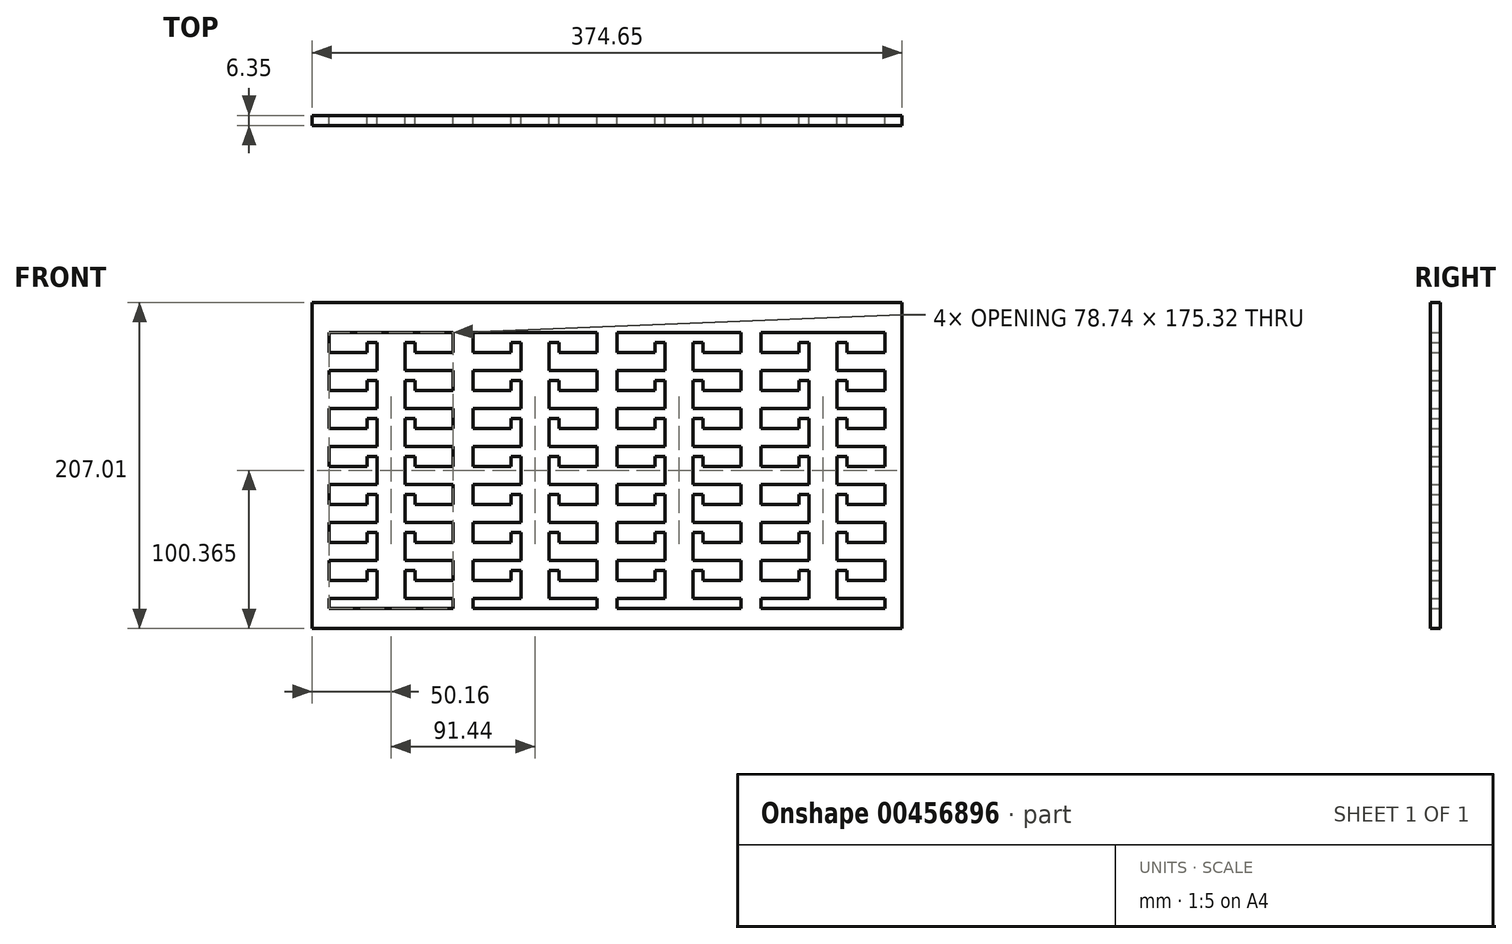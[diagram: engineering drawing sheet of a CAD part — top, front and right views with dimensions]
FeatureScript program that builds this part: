
annotation { "Feature Type Name" : "Feature", "Feature Type Description" : "" }
export const myFeature = defineFeature(function(context is Context, id is Id, definition is map)
    precondition{}
    {
        {
            var Q0;
            Q0=qCreatedBy(makeId("Front.planeOp"),FACE);
            var sketch = newSketch(context, id + "F0", { "sketchPlane" : qUnion([Q0])});
            skLineSegment(sketch, "E0", {"start": v(-92.88, -73.63) * mm, "end": v(-62.4, -73.63) * mm});
            skLineSegment(sketch, "E1", {"start": v(-62.4, -73.63) * mm, "end": v(-62.4, -55.85) * mm});
            skLineSegment(sketch, "E2", {"start": v(-62.4, -55.85) * mm, "end": v(-68.75, -55.85) * mm});
            skLineSegment(sketch, "E3", {"start": v(-68.75, -55.85) * mm, "end": v(-68.75, -62.2) * mm});
            skLineSegment(sketch, "E4", {"start": v(-68.75, -62.2) * mm, "end": v(-92.88, -62.2) * mm});
            skLineSegment(sketch, "E5", {"start": v(-92.88, -62.2) * mm, "end": v(-92.88, -49.5) * mm});
            skLineSegment(sketch, "E6", {"start": v(-92.88, -49.5) * mm, "end": v(-62.4, -49.5) * mm});
            skLineSegment(sketch, "E7", {"start": v(-62.4, -49.5) * mm, "end": v(-62.4, -31.72) * mm});
            skLineSegment(sketch, "E8", {"start": v(-62.4, -31.72) * mm, "end": v(-68.75, -31.72) * mm});
            skLineSegment(sketch, "E9", {"start": v(-68.75, -31.72) * mm, "end": v(-68.75, -38.07) * mm});
            skLineSegment(sketch, "E10", {"start": v(-68.75, -38.07) * mm, "end": v(-92.88, -38.07) * mm});
            skLineSegment(sketch, "E11", {"start": v(-92.88, -38.07) * mm, "end": v(-92.88, -25.37) * mm});
            skLineSegment(sketch, "E12", {"start": v(-92.88, -25.37) * mm, "end": v(-62.4, -25.37) * mm});
            skLineSegment(sketch, "E13", {"start": v(-62.4, -25.37) * mm, "end": v(-62.4, -7.6) * mm});
            skLineSegment(sketch, "E14", {"start": v(-62.4, -7.6) * mm, "end": v(-68.75, -7.6) * mm});
            skLineSegment(sketch, "E15", {"start": v(-68.75, -7.6) * mm, "end": v(-68.75, -13.94) * mm});
            skLineSegment(sketch, "E16", {"start": v(-68.75, -13.94) * mm, "end": v(-92.88, -13.94) * mm});
            skLineSegment(sketch, "E17", {"start": v(-92.88, -13.94) * mm, "end": v(-92.88, -1.24) * mm});
            skLineSegment(sketch, "E18", {"start": v(-92.88, -1.24) * mm, "end": v(-62.4, -1.24) * mm});
            skLineSegment(sketch, "E19", {"start": v(-62.4, -1.24) * mm, "end": v(-62.4, 16.54) * mm});
            skLineSegment(sketch, "E20", {"start": v(-62.4, 16.54) * mm, "end": v(-68.75, 16.54) * mm});
            skLineSegment(sketch, "E21", {"start": v(-68.75, 16.54) * mm, "end": v(-68.75, 10.19) * mm});
            skLineSegment(sketch, "E22", {"start": v(-68.75, 10.19) * mm, "end": v(-92.88, 10.19) * mm});
            skLineSegment(sketch, "E23", {"start": v(-92.88, 10.19) * mm, "end": v(-92.88, 22.89) * mm});
            skLineSegment(sketch, "E24", {"start": v(-92.88, 22.89) * mm, "end": v(-62.4, 22.89) * mm});
            skLineSegment(sketch, "E25", {"start": v(-62.4, 22.89) * mm, "end": v(-62.4, 40.67) * mm});
            skLineSegment(sketch, "E26", {"start": v(-62.4, 40.67) * mm, "end": v(-68.75, 40.67) * mm});
            skLineSegment(sketch, "E27", {"start": v(-68.75, 40.67) * mm, "end": v(-68.75, 34.32) * mm});
            skLineSegment(sketch, "E28", {"start": v(-68.75, 34.32) * mm, "end": v(-92.88, 34.32) * mm});
            skLineSegment(sketch, "E29", {"start": v(-92.88, 34.32) * mm, "end": v(-92.88, 47.02) * mm});
            skLineSegment(sketch, "E30", {"start": v(-92.88, 47.02) * mm, "end": v(-62.4, 47.02) * mm});
            skLineSegment(sketch, "E31", {"start": v(-62.4, 64.8) * mm, "end": v(-68.75, 64.8) * mm});
            skLineSegment(sketch, "E32", {"start": v(-68.75, 64.8) * mm, "end": v(-68.75, 58.45) * mm});
            skLineSegment(sketch, "E33", {"start": v(-68.75, 58.45) * mm, "end": v(-92.88, 58.45) * mm});
            skLineSegment(sketch, "E34", {"start": v(-92.88, 58.45) * mm, "end": v(-92.88, 71.15) * mm});
            skLineSegment(sketch, "E35", {"start": v(-14.14, -104.18) * mm, "end": v(-14.14, -97.76) * mm});
            skLineSegment(sketch, "E36", {"start": v(-14.14, -97.76) * mm, "end": v(-44.62, -97.76) * mm});
            skLineSegment(sketch, "E37", {"start": v(-44.62, -97.76) * mm, "end": v(-44.62, -79.98) * mm});
            skLineSegment(sketch, "E38", {"start": v(-44.62, -79.98) * mm, "end": v(-38.27, -79.98) * mm});
            skLineSegment(sketch, "E39", {"start": v(-38.27, -79.98) * mm, "end": v(-38.27, -86.33) * mm});
            skLineSegment(sketch, "E40", {"start": v(-38.27, -86.33) * mm, "end": v(-14.14, -86.33) * mm});
            skLineSegment(sketch, "E41", {"start": v(-14.14, -86.33) * mm, "end": v(-14.14, -73.63) * mm});
            skLineSegment(sketch, "E42", {"start": v(-14.14, -73.63) * mm, "end": v(-44.62, -73.63) * mm});
            skLineSegment(sketch, "E43", {"start": v(-44.62, -73.63) * mm, "end": v(-44.62, -55.85) * mm});
            skLineSegment(sketch, "E44", {"start": v(-44.62, -55.85) * mm, "end": v(-38.27, -55.85) * mm});
            skLineSegment(sketch, "E45", {"start": v(-38.27, -55.85) * mm, "end": v(-38.27, -62.2) * mm});
            skLineSegment(sketch, "E46", {"start": v(-38.27, -62.2) * mm, "end": v(-14.14, -62.2) * mm});
            skLineSegment(sketch, "E47", {"start": v(-14.14, -62.2) * mm, "end": v(-14.14, -49.5) * mm});
            skLineSegment(sketch, "E48", {"start": v(-14.14, -49.5) * mm, "end": v(-44.62, -49.5) * mm});
            skLineSegment(sketch, "E49", {"start": v(-44.62, -49.5) * mm, "end": v(-44.62, -31.72) * mm});
            skLineSegment(sketch, "E50", {"start": v(-44.62, -31.72) * mm, "end": v(-38.27, -31.72) * mm});
            skLineSegment(sketch, "E51", {"start": v(-38.27, -31.72) * mm, "end": v(-38.27, -38.07) * mm});
            skLineSegment(sketch, "E52", {"start": v(-38.27, -38.07) * mm, "end": v(-14.14, -38.07) * mm});
            skLineSegment(sketch, "E53", {"start": v(-14.14, -38.07) * mm, "end": v(-14.14, -25.37) * mm});
            skLineSegment(sketch, "E54", {"start": v(-14.14, -25.37) * mm, "end": v(-44.62, -25.37) * mm});
            skLineSegment(sketch, "E55", {"start": v(-44.62, -25.37) * mm, "end": v(-44.62, -7.6) * mm});
            skLineSegment(sketch, "E56", {"start": v(-44.62, -7.6) * mm, "end": v(-38.27, -7.6) * mm});
            skLineSegment(sketch, "E57", {"start": v(-38.27, -7.6) * mm, "end": v(-38.27, -13.94) * mm});
            skLineSegment(sketch, "E58", {"start": v(-38.27, -13.94) * mm, "end": v(-14.14, -13.94) * mm});
            skLineSegment(sketch, "E59", {"start": v(-14.14, -13.94) * mm, "end": v(-14.14, -1.24) * mm});
            skLineSegment(sketch, "E60", {"start": v(-14.14, -1.24) * mm, "end": v(-44.62, -1.24) * mm});
            skLineSegment(sketch, "E61", {"start": v(-44.62, -1.24) * mm, "end": v(-44.62, 16.54) * mm});
            skLineSegment(sketch, "E62", {"start": v(-44.62, 16.54) * mm, "end": v(-38.27, 16.54) * mm});
            skLineSegment(sketch, "E63", {"start": v(-38.27, 16.54) * mm, "end": v(-38.27, 10.19) * mm});
            skLineSegment(sketch, "E64", {"start": v(-38.27, 10.19) * mm, "end": v(-14.14, 10.19) * mm});
            skLineSegment(sketch, "E65", {"start": v(-14.14, 10.19) * mm, "end": v(-14.14, 22.89) * mm});
            skLineSegment(sketch, "E66", {"start": v(-14.14, 22.89) * mm, "end": v(-44.62, 22.89) * mm});
            skLineSegment(sketch, "E67", {"start": v(-44.62, 22.89) * mm, "end": v(-44.62, 40.67) * mm});
            skLineSegment(sketch, "E68", {"start": v(-44.62, 40.67) * mm, "end": v(-38.27, 40.67) * mm});
            skLineSegment(sketch, "E69", {"start": v(-38.27, 40.67) * mm, "end": v(-38.27, 34.32) * mm});
            skLineSegment(sketch, "E70", {"start": v(-38.27, 34.32) * mm, "end": v(-14.14, 34.32) * mm});
            skLineSegment(sketch, "E71", {"start": v(-14.14, 34.32) * mm, "end": v(-14.14, 47.02) * mm});
            skLineSegment(sketch, "E72", {"start": v(-14.14, 47.02) * mm, "end": v(-44.62, 47.02) * mm});
            skLineSegment(sketch, "E73", {"start": v(-44.62, 47.02) * mm, "end": v(-44.62, 64.8) * mm});
            skLineSegment(sketch, "E74", {"start": v(-44.62, 64.8) * mm, "end": v(-38.27, 64.8) * mm});
            skLineSegment(sketch, "E75", {"start": v(-38.27, 64.8) * mm, "end": v(-38.27, 58.45) * mm});
            skLineSegment(sketch, "E76", {"start": v(-38.27, 58.45) * mm, "end": v(-14.14, 58.45) * mm});
            skLineSegment(sketch, "E77", {"start": v(-14.14, 58.45) * mm, "end": v(-14.14, 71.15) * mm});
            skLineSegment(sketch, "E78", {"start": v(-62.4, 47.02) * mm, "end": v(-62.4, 64.8) * mm});
            skLineSegment(sketch, "E79", {"start": v(-62.4, -97.76) * mm, "end": v(-62.4, -79.98) * mm});
            skLineSegment(sketch, "E80", {"start": v(-68.75, -86.33) * mm, "end": v(-68.75, -79.98) * mm});
            skLineSegment(sketch, "E81", {"start": v(-68.75, -79.98) * mm, "end": v(-62.4, -79.98) * mm});
            skLineSegment(sketch, "E82", {"start": v(-62.4, -97.76) * mm, "end": v(-92.88, -97.76) * mm});
            skLineSegment(sketch, "E83", {"start": v(-92.88, -86.33) * mm, "end": v(-92.88, -73.63) * mm});
            skLineSegment(sketch, "E84", {"start": v(-92.88, -97.76) * mm, "end": v(-92.88, -104.18) * mm});
            skLineSegment(sketch, "E85", {"start": v(-92.88, -86.33) * mm, "end": v(-68.75, -86.33) * mm});
            skLineSegment(sketch, "E86", {"start": v(-92.88, -104.18) * mm, "end": v(-14.14, -104.18) * mm});
            skLineSegment(sketch, "E87", {"start": v(-92.88, 71.15) * mm, "end": v(-14.14, 71.15) * mm});
            skPoint(sketch, "E88", {"position": v(-53.5, 71.15) * mm});
            skPoint(sketch, "E89", {"position": v(-53.5, -104.18) * mm});
            skLineSegment(sketch, "E90", {"start": v(-184.32, -73.63) * mm, "end": v(-153.84, -73.63) * mm});
            skLineSegment(sketch, "E91", {"start": v(-153.84, -73.63) * mm, "end": v(-153.84, -55.85) * mm});
            skLineSegment(sketch, "E92", {"start": v(-153.84, -55.85) * mm, "end": v(-160.19, -55.85) * mm});
            skLineSegment(sketch, "E93", {"start": v(-160.19, -55.85) * mm, "end": v(-160.19, -62.2) * mm});
            skLineSegment(sketch, "E94", {"start": v(-160.19, -62.2) * mm, "end": v(-184.32, -62.2) * mm});
            skLineSegment(sketch, "E95", {"start": v(-184.32, -62.2) * mm, "end": v(-184.32, -49.5) * mm});
            skLineSegment(sketch, "E96", {"start": v(-184.32, -49.5) * mm, "end": v(-153.84, -49.5) * mm});
            skLineSegment(sketch, "E97", {"start": v(-153.84, -49.5) * mm, "end": v(-153.84, -31.72) * mm});
            skLineSegment(sketch, "E98", {"start": v(-153.84, -31.72) * mm, "end": v(-160.19, -31.72) * mm});
            skLineSegment(sketch, "E99", {"start": v(-160.19, -31.72) * mm, "end": v(-160.19, -38.07) * mm});
            skLineSegment(sketch, "E100", {"start": v(-160.19, -38.07) * mm, "end": v(-184.32, -38.07) * mm});
            skLineSegment(sketch, "E101", {"start": v(-184.32, -38.07) * mm, "end": v(-184.32, -25.37) * mm});
            skLineSegment(sketch, "E102", {"start": v(-184.32, -25.37) * mm, "end": v(-153.84, -25.37) * mm});
            skLineSegment(sketch, "E103", {"start": v(-153.84, -25.37) * mm, "end": v(-153.84, -7.6) * mm});
            skLineSegment(sketch, "E104", {"start": v(-153.84, -7.6) * mm, "end": v(-160.19, -7.6) * mm});
            skLineSegment(sketch, "E105", {"start": v(-160.19, -7.6) * mm, "end": v(-160.19, -13.94) * mm});
            skLineSegment(sketch, "E106", {"start": v(-160.19, -13.94) * mm, "end": v(-184.32, -13.94) * mm});
            skLineSegment(sketch, "E107", {"start": v(-184.32, -13.94) * mm, "end": v(-184.32, -1.24) * mm});
            skLineSegment(sketch, "E108", {"start": v(-184.32, -1.24) * mm, "end": v(-153.84, -1.24) * mm});
            skLineSegment(sketch, "E109", {"start": v(-153.84, -1.24) * mm, "end": v(-153.84, 16.54) * mm});
            skLineSegment(sketch, "E110", {"start": v(-153.84, 16.54) * mm, "end": v(-160.19, 16.54) * mm});
            skLineSegment(sketch, "E111", {"start": v(-160.19, 16.54) * mm, "end": v(-160.19, 10.19) * mm});
            skLineSegment(sketch, "E112", {"start": v(-160.19, 10.19) * mm, "end": v(-184.32, 10.19) * mm});
            skLineSegment(sketch, "E113", {"start": v(-184.32, 10.19) * mm, "end": v(-184.32, 22.89) * mm});
            skLineSegment(sketch, "E114", {"start": v(-184.32, 22.89) * mm, "end": v(-153.84, 22.89) * mm});
            skLineSegment(sketch, "E115", {"start": v(-153.84, 22.89) * mm, "end": v(-153.84, 40.67) * mm});
            skLineSegment(sketch, "E116", {"start": v(-153.84, 40.67) * mm, "end": v(-160.19, 40.67) * mm});
            skLineSegment(sketch, "E117", {"start": v(-160.19, 40.67) * mm, "end": v(-160.19, 34.32) * mm});
            skLineSegment(sketch, "E118", {"start": v(-160.19, 34.32) * mm, "end": v(-184.32, 34.32) * mm});
            skLineSegment(sketch, "E119", {"start": v(-184.32, 34.32) * mm, "end": v(-184.32, 47.02) * mm});
            skLineSegment(sketch, "E120", {"start": v(-184.32, 47.02) * mm, "end": v(-153.84, 47.02) * mm});
            skLineSegment(sketch, "E121", {"start": v(-153.84, 64.8) * mm, "end": v(-160.19, 64.8) * mm});
            skLineSegment(sketch, "E122", {"start": v(-160.19, 64.8) * mm, "end": v(-160.19, 58.45) * mm});
            skLineSegment(sketch, "E123", {"start": v(-160.19, 58.45) * mm, "end": v(-184.32, 58.45) * mm});
            skLineSegment(sketch, "E124", {"start": v(-184.32, 58.45) * mm, "end": v(-184.32, 71.15) * mm});
            skLineSegment(sketch, "E125", {"start": v(-105.58, -104.18) * mm, "end": v(-105.58, -97.76) * mm});
            skLineSegment(sketch, "E126", {"start": v(-105.58, -97.76) * mm, "end": v(-136.06, -97.76) * mm});
            skLineSegment(sketch, "E127", {"start": v(-136.06, -97.76) * mm, "end": v(-136.06, -79.98) * mm});
            skLineSegment(sketch, "E128", {"start": v(-136.06, -79.98) * mm, "end": v(-129.7, -79.98) * mm});
            skLineSegment(sketch, "E129", {"start": v(-129.7, -79.98) * mm, "end": v(-129.7, -86.33) * mm});
            skLineSegment(sketch, "E130", {"start": v(-129.7, -86.33) * mm, "end": v(-105.58, -86.33) * mm});
            skLineSegment(sketch, "E131", {"start": v(-105.58, -86.33) * mm, "end": v(-105.58, -73.63) * mm});
            skLineSegment(sketch, "E132", {"start": v(-105.58, -73.63) * mm, "end": v(-136.06, -73.63) * mm});
            skLineSegment(sketch, "E133", {"start": v(-136.06, -73.63) * mm, "end": v(-136.06, -55.85) * mm});
            skLineSegment(sketch, "E134", {"start": v(-136.06, -55.85) * mm, "end": v(-129.7, -55.85) * mm});
            skLineSegment(sketch, "E135", {"start": v(-129.7, -55.85) * mm, "end": v(-129.7, -62.2) * mm});
            skLineSegment(sketch, "E136", {"start": v(-129.7, -62.2) * mm, "end": v(-105.58, -62.2) * mm});
            skLineSegment(sketch, "E137", {"start": v(-105.58, -62.2) * mm, "end": v(-105.58, -49.5) * mm});
            skLineSegment(sketch, "E138", {"start": v(-105.58, -49.5) * mm, "end": v(-136.06, -49.5) * mm});
            skLineSegment(sketch, "E139", {"start": v(-136.06, -49.5) * mm, "end": v(-136.06, -31.72) * mm});
            skLineSegment(sketch, "E140", {"start": v(-136.06, -31.72) * mm, "end": v(-129.7, -31.72) * mm});
            skLineSegment(sketch, "E141", {"start": v(-129.7, -31.72) * mm, "end": v(-129.7, -38.07) * mm});
            skLineSegment(sketch, "E142", {"start": v(-129.7, -38.07) * mm, "end": v(-105.58, -38.07) * mm});
            skLineSegment(sketch, "E143", {"start": v(-105.58, -38.07) * mm, "end": v(-105.58, -25.37) * mm});
            skLineSegment(sketch, "E144", {"start": v(-105.58, -25.37) * mm, "end": v(-136.06, -25.37) * mm});
            skLineSegment(sketch, "E145", {"start": v(-136.06, -25.37) * mm, "end": v(-136.06, -7.6) * mm});
            skLineSegment(sketch, "E146", {"start": v(-136.06, -7.6) * mm, "end": v(-129.7, -7.6) * mm});
            skLineSegment(sketch, "E147", {"start": v(-129.7, -7.6) * mm, "end": v(-129.7, -13.94) * mm});
            skLineSegment(sketch, "E148", {"start": v(-129.7, -13.94) * mm, "end": v(-105.58, -13.94) * mm});
            skLineSegment(sketch, "E149", {"start": v(-105.58, -13.94) * mm, "end": v(-105.58, -1.24) * mm});
            skLineSegment(sketch, "E150", {"start": v(-105.58, -1.24) * mm, "end": v(-136.06, -1.24) * mm});
            skLineSegment(sketch, "E151", {"start": v(-136.06, -1.24) * mm, "end": v(-136.06, 16.54) * mm});
            skLineSegment(sketch, "E152", {"start": v(-136.06, 16.54) * mm, "end": v(-129.7, 16.54) * mm});
            skLineSegment(sketch, "E153", {"start": v(-129.7, 16.54) * mm, "end": v(-129.7, 10.19) * mm});
            skLineSegment(sketch, "E154", {"start": v(-129.7, 10.19) * mm, "end": v(-105.58, 10.19) * mm});
            skLineSegment(sketch, "E155", {"start": v(-105.58, 10.19) * mm, "end": v(-105.58, 22.89) * mm});
            skLineSegment(sketch, "E156", {"start": v(-105.58, 22.89) * mm, "end": v(-136.06, 22.89) * mm});
            skLineSegment(sketch, "E157", {"start": v(-136.06, 22.89) * mm, "end": v(-136.06, 40.67) * mm});
            skLineSegment(sketch, "E158", {"start": v(-136.06, 40.67) * mm, "end": v(-129.7, 40.67) * mm});
            skLineSegment(sketch, "E159", {"start": v(-129.7, 40.67) * mm, "end": v(-129.7, 34.32) * mm});
            skLineSegment(sketch, "E160", {"start": v(-129.7, 34.32) * mm, "end": v(-105.58, 34.32) * mm});
            skLineSegment(sketch, "E161", {"start": v(-105.58, 34.32) * mm, "end": v(-105.58, 47.02) * mm});
            skLineSegment(sketch, "E162", {"start": v(-105.58, 47.02) * mm, "end": v(-136.06, 47.02) * mm});
            skLineSegment(sketch, "E163", {"start": v(-136.06, 47.02) * mm, "end": v(-136.06, 64.8) * mm});
            skLineSegment(sketch, "E164", {"start": v(-136.06, 64.8) * mm, "end": v(-129.7, 64.8) * mm});
            skLineSegment(sketch, "E165", {"start": v(-129.7, 64.8) * mm, "end": v(-129.7, 58.45) * mm});
            skLineSegment(sketch, "E166", {"start": v(-129.7, 58.45) * mm, "end": v(-105.58, 58.45) * mm});
            skLineSegment(sketch, "E167", {"start": v(-105.58, 58.45) * mm, "end": v(-105.58, 71.15) * mm});
            skLineSegment(sketch, "E168", {"start": v(-153.84, 47.02) * mm, "end": v(-153.84, 64.8) * mm});
            skLineSegment(sketch, "E169", {"start": v(-153.84, -97.76) * mm, "end": v(-153.84, -79.98) * mm});
            skLineSegment(sketch, "E170", {"start": v(-160.19, -86.33) * mm, "end": v(-160.19, -79.98) * mm});
            skLineSegment(sketch, "E171", {"start": v(-160.19, -79.98) * mm, "end": v(-153.84, -79.98) * mm});
            skLineSegment(sketch, "E172", {"start": v(-153.84, -97.76) * mm, "end": v(-184.32, -97.76) * mm});
            skLineSegment(sketch, "E173", {"start": v(-184.32, -86.33) * mm, "end": v(-184.32, -73.63) * mm});
            skLineSegment(sketch, "E174", {"start": v(-184.32, -97.76) * mm, "end": v(-184.32, -104.18) * mm});
            skLineSegment(sketch, "E175", {"start": v(-184.32, -86.33) * mm, "end": v(-160.19, -86.33) * mm});
            skLineSegment(sketch, "E176", {"start": v(-184.32, -104.18) * mm, "end": v(-105.58, -104.18) * mm});
            skLineSegment(sketch, "E177", {"start": v(-184.32, 71.15) * mm, "end": v(-105.58, 71.15) * mm});
            skPoint(sketch, "E178", {"position": v(-144.95, 71.15) * mm});
            skPoint(sketch, "E179", {"position": v(-144.95, -104.18) * mm});
            skLineSegment(sketch, "E180", {"start": v(-275.76, -73.63) * mm, "end": v(-245.28, -73.63) * mm});
            skLineSegment(sketch, "E181", {"start": v(-245.28, -73.63) * mm, "end": v(-245.28, -55.85) * mm});
            skLineSegment(sketch, "E182", {"start": v(-245.28, -55.85) * mm, "end": v(-251.63, -55.85) * mm});
            skLineSegment(sketch, "E183", {"start": v(-251.63, -55.85) * mm, "end": v(-251.63, -62.2) * mm});
            skLineSegment(sketch, "E184", {"start": v(-251.63, -62.2) * mm, "end": v(-275.76, -62.2) * mm});
            skLineSegment(sketch, "E185", {"start": v(-275.76, -62.2) * mm, "end": v(-275.76, -49.5) * mm});
            skLineSegment(sketch, "E186", {"start": v(-275.76, -49.5) * mm, "end": v(-245.28, -49.5) * mm});
            skLineSegment(sketch, "E187", {"start": v(-245.28, -49.5) * mm, "end": v(-245.28, -31.72) * mm});
            skLineSegment(sketch, "E188", {"start": v(-245.28, -31.72) * mm, "end": v(-251.63, -31.72) * mm});
            skLineSegment(sketch, "E189", {"start": v(-251.63, -31.72) * mm, "end": v(-251.63, -38.07) * mm});
            skLineSegment(sketch, "E190", {"start": v(-251.63, -38.07) * mm, "end": v(-275.76, -38.07) * mm});
            skLineSegment(sketch, "E191", {"start": v(-275.76, -38.07) * mm, "end": v(-275.76, -25.37) * mm});
            skLineSegment(sketch, "E192", {"start": v(-275.76, -25.37) * mm, "end": v(-245.28, -25.37) * mm});
            skLineSegment(sketch, "E193", {"start": v(-245.28, -25.37) * mm, "end": v(-245.28, -7.6) * mm});
            skLineSegment(sketch, "E194", {"start": v(-245.28, -7.6) * mm, "end": v(-251.63, -7.6) * mm});
            skLineSegment(sketch, "E195", {"start": v(-251.63, -7.6) * mm, "end": v(-251.63, -13.94) * mm});
            skLineSegment(sketch, "E196", {"start": v(-251.63, -13.94) * mm, "end": v(-275.76, -13.94) * mm});
            skLineSegment(sketch, "E197", {"start": v(-275.76, -13.94) * mm, "end": v(-275.76, -1.24) * mm});
            skLineSegment(sketch, "E198", {"start": v(-275.76, -1.24) * mm, "end": v(-245.28, -1.24) * mm});
            skLineSegment(sketch, "E199", {"start": v(-245.28, -1.24) * mm, "end": v(-245.28, 16.54) * mm});
            skLineSegment(sketch, "E200", {"start": v(-245.28, 16.54) * mm, "end": v(-251.63, 16.54) * mm});
            skLineSegment(sketch, "E201", {"start": v(-251.63, 16.54) * mm, "end": v(-251.63, 10.19) * mm});
            skLineSegment(sketch, "E202", {"start": v(-251.63, 10.19) * mm, "end": v(-275.76, 10.19) * mm});
            skLineSegment(sketch, "E203", {"start": v(-275.76, 10.19) * mm, "end": v(-275.76, 22.89) * mm});
            skLineSegment(sketch, "E204", {"start": v(-275.76, 22.89) * mm, "end": v(-245.28, 22.89) * mm});
            skLineSegment(sketch, "E205", {"start": v(-245.28, 22.89) * mm, "end": v(-245.28, 40.67) * mm});
            skLineSegment(sketch, "E206", {"start": v(-245.28, 40.67) * mm, "end": v(-251.63, 40.67) * mm});
            skLineSegment(sketch, "E207", {"start": v(-251.63, 40.67) * mm, "end": v(-251.63, 34.32) * mm});
            skLineSegment(sketch, "E208", {"start": v(-251.63, 34.32) * mm, "end": v(-275.76, 34.32) * mm});
            skLineSegment(sketch, "E209", {"start": v(-275.76, 34.32) * mm, "end": v(-275.76, 47.02) * mm});
            skLineSegment(sketch, "E210", {"start": v(-275.76, 47.02) * mm, "end": v(-245.28, 47.02) * mm});
            skLineSegment(sketch, "E211", {"start": v(-245.28, 64.8) * mm, "end": v(-251.63, 64.8) * mm});
            skLineSegment(sketch, "E212", {"start": v(-251.63, 64.8) * mm, "end": v(-251.63, 58.45) * mm});
            skLineSegment(sketch, "E213", {"start": v(-251.63, 58.45) * mm, "end": v(-275.76, 58.45) * mm});
            skLineSegment(sketch, "E214", {"start": v(-275.76, 58.45) * mm, "end": v(-275.76, 71.15) * mm});
            skLineSegment(sketch, "E215", {"start": v(-197.02, -104.18) * mm, "end": v(-197.02, -97.76) * mm});
            skLineSegment(sketch, "E216", {"start": v(-197.02, -97.76) * mm, "end": v(-227.5, -97.76) * mm});
            skLineSegment(sketch, "E217", {"start": v(-227.5, -97.76) * mm, "end": v(-227.5, -79.98) * mm});
            skLineSegment(sketch, "E218", {"start": v(-227.5, -79.98) * mm, "end": v(-221.15, -79.98) * mm});
            skLineSegment(sketch, "E219", {"start": v(-221.15, -79.98) * mm, "end": v(-221.15, -86.33) * mm});
            skLineSegment(sketch, "E220", {"start": v(-221.15, -86.33) * mm, "end": v(-197.02, -86.33) * mm});
            skLineSegment(sketch, "E221", {"start": v(-197.02, -86.33) * mm, "end": v(-197.02, -73.63) * mm});
            skLineSegment(sketch, "E222", {"start": v(-197.02, -73.63) * mm, "end": v(-227.5, -73.63) * mm});
            skLineSegment(sketch, "E223", {"start": v(-227.5, -73.63) * mm, "end": v(-227.5, -55.85) * mm});
            skLineSegment(sketch, "E224", {"start": v(-227.5, -55.85) * mm, "end": v(-221.15, -55.85) * mm});
            skLineSegment(sketch, "E225", {"start": v(-221.15, -55.85) * mm, "end": v(-221.15, -62.2) * mm});
            skLineSegment(sketch, "E226", {"start": v(-221.15, -62.2) * mm, "end": v(-197.02, -62.2) * mm});
            skLineSegment(sketch, "E227", {"start": v(-197.02, -62.2) * mm, "end": v(-197.02, -49.5) * mm});
            skLineSegment(sketch, "E228", {"start": v(-197.02, -49.5) * mm, "end": v(-227.5, -49.5) * mm});
            skLineSegment(sketch, "E229", {"start": v(-227.5, -49.5) * mm, "end": v(-227.5, -31.72) * mm});
            skLineSegment(sketch, "E230", {"start": v(-227.5, -31.72) * mm, "end": v(-221.15, -31.72) * mm});
            skLineSegment(sketch, "E231", {"start": v(-221.15, -31.72) * mm, "end": v(-221.15, -38.07) * mm});
            skLineSegment(sketch, "E232", {"start": v(-221.15, -38.07) * mm, "end": v(-197.02, -38.07) * mm});
            skLineSegment(sketch, "E233", {"start": v(-197.02, -38.07) * mm, "end": v(-197.02, -25.37) * mm});
            skLineSegment(sketch, "E234", {"start": v(-197.02, -25.37) * mm, "end": v(-227.5, -25.37) * mm});
            skLineSegment(sketch, "E235", {"start": v(-227.5, -25.37) * mm, "end": v(-227.5, -7.6) * mm});
            skLineSegment(sketch, "E236", {"start": v(-227.5, -7.6) * mm, "end": v(-221.15, -7.6) * mm});
            skLineSegment(sketch, "E237", {"start": v(-221.15, -7.6) * mm, "end": v(-221.15, -13.94) * mm});
            skLineSegment(sketch, "E238", {"start": v(-221.15, -13.94) * mm, "end": v(-197.02, -13.94) * mm});
            skLineSegment(sketch, "E239", {"start": v(-197.02, -13.94) * mm, "end": v(-197.02, -1.24) * mm});
            skLineSegment(sketch, "E240", {"start": v(-197.02, -1.24) * mm, "end": v(-227.5, -1.24) * mm});
            skLineSegment(sketch, "E241", {"start": v(-227.5, -1.24) * mm, "end": v(-227.5, 16.54) * mm});
            skLineSegment(sketch, "E242", {"start": v(-227.5, 16.54) * mm, "end": v(-221.15, 16.54) * mm});
            skLineSegment(sketch, "E243", {"start": v(-221.15, 16.54) * mm, "end": v(-221.15, 10.19) * mm});
            skLineSegment(sketch, "E244", {"start": v(-221.15, 10.19) * mm, "end": v(-197.02, 10.19) * mm});
            skLineSegment(sketch, "E245", {"start": v(-197.02, 10.19) * mm, "end": v(-197.02, 22.89) * mm});
            skLineSegment(sketch, "E246", {"start": v(-197.02, 22.89) * mm, "end": v(-227.5, 22.89) * mm});
            skLineSegment(sketch, "E247", {"start": v(-227.5, 22.89) * mm, "end": v(-227.5, 40.67) * mm});
            skLineSegment(sketch, "E248", {"start": v(-227.5, 40.67) * mm, "end": v(-221.15, 40.67) * mm});
            skLineSegment(sketch, "E249", {"start": v(-221.15, 40.67) * mm, "end": v(-221.15, 34.32) * mm});
            skLineSegment(sketch, "E250", {"start": v(-221.15, 34.32) * mm, "end": v(-197.02, 34.32) * mm});
            skLineSegment(sketch, "E251", {"start": v(-197.02, 34.32) * mm, "end": v(-197.02, 47.02) * mm});
            skLineSegment(sketch, "E252", {"start": v(-197.02, 47.02) * mm, "end": v(-227.5, 47.02) * mm});
            skLineSegment(sketch, "E253", {"start": v(-227.5, 47.02) * mm, "end": v(-227.5, 64.8) * mm});
            skLineSegment(sketch, "E254", {"start": v(-227.5, 64.8) * mm, "end": v(-221.15, 64.8) * mm});
            skLineSegment(sketch, "E255", {"start": v(-221.15, 64.8) * mm, "end": v(-221.15, 58.45) * mm});
            skLineSegment(sketch, "E256", {"start": v(-221.15, 58.45) * mm, "end": v(-197.02, 58.45) * mm});
            skLineSegment(sketch, "E257", {"start": v(-197.02, 58.45) * mm, "end": v(-197.02, 71.15) * mm});
            skLineSegment(sketch, "E258", {"start": v(-245.28, 47.02) * mm, "end": v(-245.28, 64.8) * mm});
            skLineSegment(sketch, "E259", {"start": v(-245.28, -97.76) * mm, "end": v(-245.28, -79.98) * mm});
            skLineSegment(sketch, "E260", {"start": v(-251.63, -86.33) * mm, "end": v(-251.63, -79.98) * mm});
            skLineSegment(sketch, "E261", {"start": v(-251.63, -79.98) * mm, "end": v(-245.28, -79.98) * mm});
            skLineSegment(sketch, "E262", {"start": v(-245.28, -97.76) * mm, "end": v(-275.76, -97.76) * mm});
            skLineSegment(sketch, "E263", {"start": v(-275.76, -86.33) * mm, "end": v(-275.76, -73.63) * mm});
            skLineSegment(sketch, "E264", {"start": v(-275.76, -97.76) * mm, "end": v(-275.76, -104.18) * mm});
            skLineSegment(sketch, "E265", {"start": v(-275.76, -86.33) * mm, "end": v(-251.63, -86.33) * mm});
            skLineSegment(sketch, "E266", {"start": v(-275.76, -104.18) * mm, "end": v(-197.02, -104.18) * mm});
            skLineSegment(sketch, "E267", {"start": v(-275.76, 71.15) * mm, "end": v(-197.02, 71.15) * mm});
            skPoint(sketch, "E268", {"position": v(-236.39, 71.15) * mm});
            skPoint(sketch, "E269", {"position": v(-236.39, -104.18) * mm});
            skLineSegment(sketch, "E270", {"start": v(-367.2, -73.63) * mm, "end": v(-336.72, -73.63) * mm});
            skLineSegment(sketch, "E271", {"start": v(-336.72, -73.63) * mm, "end": v(-336.72, -55.85) * mm});
            skLineSegment(sketch, "E272", {"start": v(-336.72, -55.85) * mm, "end": v(-343.07, -55.85) * mm});
            skLineSegment(sketch, "E273", {"start": v(-343.07, -55.85) * mm, "end": v(-343.07, -62.2) * mm});
            skLineSegment(sketch, "E274", {"start": v(-343.07, -62.2) * mm, "end": v(-367.2, -62.2) * mm});
            skLineSegment(sketch, "E275", {"start": v(-367.2, -62.2) * mm, "end": v(-367.2, -49.5) * mm});
            skLineSegment(sketch, "E276", {"start": v(-367.2, -49.5) * mm, "end": v(-336.72, -49.5) * mm});
            skLineSegment(sketch, "E277", {"start": v(-336.72, -49.5) * mm, "end": v(-336.72, -31.72) * mm});
            skLineSegment(sketch, "E278", {"start": v(-336.72, -31.72) * mm, "end": v(-343.07, -31.72) * mm});
            skLineSegment(sketch, "E279", {"start": v(-343.07, -31.72) * mm, "end": v(-343.07, -38.07) * mm});
            skLineSegment(sketch, "E280", {"start": v(-343.07, -38.07) * mm, "end": v(-367.2, -38.07) * mm});
            skLineSegment(sketch, "E281", {"start": v(-367.2, -38.07) * mm, "end": v(-367.2, -25.37) * mm});
            skLineSegment(sketch, "E282", {"start": v(-367.2, -25.37) * mm, "end": v(-336.72, -25.37) * mm});
            skLineSegment(sketch, "E283", {"start": v(-336.72, -25.37) * mm, "end": v(-336.72, -7.6) * mm});
            skLineSegment(sketch, "E284", {"start": v(-336.72, -7.6) * mm, "end": v(-343.07, -7.6) * mm});
            skLineSegment(sketch, "E285", {"start": v(-343.07, -7.6) * mm, "end": v(-343.07, -13.94) * mm});
            skLineSegment(sketch, "E286", {"start": v(-343.07, -13.94) * mm, "end": v(-367.2, -13.94) * mm});
            skLineSegment(sketch, "E287", {"start": v(-367.2, -13.94) * mm, "end": v(-367.2, -1.24) * mm});
            skLineSegment(sketch, "E288", {"start": v(-367.2, -1.24) * mm, "end": v(-336.72, -1.24) * mm});
            skLineSegment(sketch, "E289", {"start": v(-336.72, -1.24) * mm, "end": v(-336.72, 16.54) * mm});
            skLineSegment(sketch, "E290", {"start": v(-336.72, 16.54) * mm, "end": v(-343.07, 16.54) * mm});
            skLineSegment(sketch, "E291", {"start": v(-343.07, 16.54) * mm, "end": v(-343.07, 10.19) * mm});
            skLineSegment(sketch, "E292", {"start": v(-343.07, 10.19) * mm, "end": v(-367.2, 10.19) * mm});
            skLineSegment(sketch, "E293", {"start": v(-367.2, 10.19) * mm, "end": v(-367.2, 22.89) * mm});
            skLineSegment(sketch, "E294", {"start": v(-367.2, 22.89) * mm, "end": v(-336.72, 22.89) * mm});
            skLineSegment(sketch, "E295", {"start": v(-336.72, 22.89) * mm, "end": v(-336.72, 40.67) * mm});
            skLineSegment(sketch, "E296", {"start": v(-336.72, 40.67) * mm, "end": v(-343.07, 40.67) * mm});
            skLineSegment(sketch, "E297", {"start": v(-343.07, 40.67) * mm, "end": v(-343.07, 34.32) * mm});
            skLineSegment(sketch, "E298", {"start": v(-343.07, 34.32) * mm, "end": v(-367.2, 34.32) * mm});
            skLineSegment(sketch, "E299", {"start": v(-367.2, 34.32) * mm, "end": v(-367.2, 47.02) * mm});
            skLineSegment(sketch, "E300", {"start": v(-367.2, 47.02) * mm, "end": v(-336.72, 47.02) * mm});
            skLineSegment(sketch, "E301", {"start": v(-336.72, 64.8) * mm, "end": v(-343.07, 64.8) * mm});
            skLineSegment(sketch, "E302", {"start": v(-343.07, 64.8) * mm, "end": v(-343.07, 58.45) * mm});
            skLineSegment(sketch, "E303", {"start": v(-343.07, 58.45) * mm, "end": v(-367.2, 58.45) * mm});
            skLineSegment(sketch, "E304", {"start": v(-367.2, 58.45) * mm, "end": v(-367.2, 71.15) * mm});
            skLineSegment(sketch, "E305", {"start": v(-288.46, -104.18) * mm, "end": v(-288.46, -97.76) * mm});
            skLineSegment(sketch, "E306", {"start": v(-288.46, -97.76) * mm, "end": v(-318.94, -97.76) * mm});
            skLineSegment(sketch, "E307", {"start": v(-318.94, -97.76) * mm, "end": v(-318.94, -79.98) * mm});
            skLineSegment(sketch, "E308", {"start": v(-318.94, -79.98) * mm, "end": v(-312.59, -79.98) * mm});
            skLineSegment(sketch, "E309", {"start": v(-312.59, -79.98) * mm, "end": v(-312.59, -86.33) * mm});
            skLineSegment(sketch, "E310", {"start": v(-312.59, -86.33) * mm, "end": v(-288.46, -86.33) * mm});
            skLineSegment(sketch, "E311", {"start": v(-288.46, -86.33) * mm, "end": v(-288.46, -73.63) * mm});
            skLineSegment(sketch, "E312", {"start": v(-288.46, -73.63) * mm, "end": v(-318.94, -73.63) * mm});
            skLineSegment(sketch, "E313", {"start": v(-318.94, -73.63) * mm, "end": v(-318.94, -55.85) * mm});
            skLineSegment(sketch, "E314", {"start": v(-318.94, -55.85) * mm, "end": v(-312.59, -55.85) * mm});
            skLineSegment(sketch, "E315", {"start": v(-312.59, -55.85) * mm, "end": v(-312.59, -62.2) * mm});
            skLineSegment(sketch, "E316", {"start": v(-312.59, -62.2) * mm, "end": v(-288.46, -62.2) * mm});
            skLineSegment(sketch, "E317", {"start": v(-288.46, -62.2) * mm, "end": v(-288.46, -49.5) * mm});
            skLineSegment(sketch, "E318", {"start": v(-288.46, -49.5) * mm, "end": v(-318.94, -49.5) * mm});
            skLineSegment(sketch, "E319", {"start": v(-318.94, -49.5) * mm, "end": v(-318.94, -31.72) * mm});
            skLineSegment(sketch, "E320", {"start": v(-318.94, -31.72) * mm, "end": v(-312.59, -31.72) * mm});
            skLineSegment(sketch, "E321", {"start": v(-312.59, -31.72) * mm, "end": v(-312.59, -38.07) * mm});
            skLineSegment(sketch, "E322", {"start": v(-312.59, -38.07) * mm, "end": v(-288.46, -38.07) * mm});
            skLineSegment(sketch, "E323", {"start": v(-288.46, -38.07) * mm, "end": v(-288.46, -25.37) * mm});
            skLineSegment(sketch, "E324", {"start": v(-288.46, -25.37) * mm, "end": v(-318.94, -25.37) * mm});
            skLineSegment(sketch, "E325", {"start": v(-318.94, -25.37) * mm, "end": v(-318.94, -7.6) * mm});
            skLineSegment(sketch, "E326", {"start": v(-318.94, -7.6) * mm, "end": v(-312.59, -7.6) * mm});
            skLineSegment(sketch, "E327", {"start": v(-312.59, -7.6) * mm, "end": v(-312.59, -13.94) * mm});
            skLineSegment(sketch, "E328", {"start": v(-312.59, -13.94) * mm, "end": v(-288.46, -13.94) * mm});
            skLineSegment(sketch, "E329", {"start": v(-288.46, -13.94) * mm, "end": v(-288.46, -1.24) * mm});
            skLineSegment(sketch, "E330", {"start": v(-288.46, -1.24) * mm, "end": v(-318.94, -1.24) * mm});
            skLineSegment(sketch, "E331", {"start": v(-318.94, -1.24) * mm, "end": v(-318.94, 16.54) * mm});
            skLineSegment(sketch, "E332", {"start": v(-318.94, 16.54) * mm, "end": v(-312.59, 16.54) * mm});
            skLineSegment(sketch, "E333", {"start": v(-312.59, 16.54) * mm, "end": v(-312.59, 10.19) * mm});
            skLineSegment(sketch, "E334", {"start": v(-312.59, 10.19) * mm, "end": v(-288.46, 10.19) * mm});
            skLineSegment(sketch, "E335", {"start": v(-288.46, 10.19) * mm, "end": v(-288.46, 22.89) * mm});
            skLineSegment(sketch, "E336", {"start": v(-288.46, 22.89) * mm, "end": v(-318.94, 22.89) * mm});
            skLineSegment(sketch, "E337", {"start": v(-318.94, 22.89) * mm, "end": v(-318.94, 40.67) * mm});
            skLineSegment(sketch, "E338", {"start": v(-318.94, 40.67) * mm, "end": v(-312.59, 40.67) * mm});
            skLineSegment(sketch, "E339", {"start": v(-312.59, 40.67) * mm, "end": v(-312.59, 34.32) * mm});
            skLineSegment(sketch, "E340", {"start": v(-312.59, 34.32) * mm, "end": v(-288.46, 34.32) * mm});
            skLineSegment(sketch, "E341", {"start": v(-288.46, 34.32) * mm, "end": v(-288.46, 47.02) * mm});
            skLineSegment(sketch, "E342", {"start": v(-288.46, 47.02) * mm, "end": v(-318.94, 47.02) * mm});
            skLineSegment(sketch, "E343", {"start": v(-318.94, 47.02) * mm, "end": v(-318.94, 64.8) * mm});
            skLineSegment(sketch, "E344", {"start": v(-318.94, 64.8) * mm, "end": v(-312.59, 64.8) * mm});
            skLineSegment(sketch, "E345", {"start": v(-312.59, 64.8) * mm, "end": v(-312.59, 58.45) * mm});
            skLineSegment(sketch, "E346", {"start": v(-312.59, 58.45) * mm, "end": v(-288.46, 58.45) * mm});
            skLineSegment(sketch, "E347", {"start": v(-288.46, 58.45) * mm, "end": v(-288.46, 71.15) * mm});
            skLineSegment(sketch, "E348", {"start": v(-336.72, 47.02) * mm, "end": v(-336.72, 64.8) * mm});
            skLineSegment(sketch, "E349", {"start": v(-336.72, -97.76) * mm, "end": v(-336.72, -79.98) * mm});
            skLineSegment(sketch, "E350", {"start": v(-343.07, -86.33) * mm, "end": v(-343.07, -79.98) * mm});
            skLineSegment(sketch, "E351", {"start": v(-343.07, -79.98) * mm, "end": v(-336.72, -79.98) * mm});
            skLineSegment(sketch, "E352", {"start": v(-336.72, -97.76) * mm, "end": v(-367.2, -97.76) * mm});
            skLineSegment(sketch, "E353", {"start": v(-367.2, -86.33) * mm, "end": v(-367.2, -73.63) * mm});
            skLineSegment(sketch, "E354", {"start": v(-367.2, -97.76) * mm, "end": v(-367.2, -104.18) * mm});
            skLineSegment(sketch, "E355", {"start": v(-367.2, -86.33) * mm, "end": v(-343.07, -86.33) * mm});
            skLineSegment(sketch, "E356", {"start": v(-367.2, -104.18) * mm, "end": v(-288.46, -104.18) * mm});
            skLineSegment(sketch, "E357", {"start": v(-367.2, 71.15) * mm, "end": v(-288.46, 71.15) * mm});
            skPoint(sketch, "E358", {"position": v(-327.83, 71.15) * mm});
            skPoint(sketch, "E359", {"position": v(-327.83, -104.18) * mm});
            skLineSegment(sketch, "E360.bottom", {"start": v(-3.34, 90.13) * mm, "end": v(-378, 90.13) * mm});
            skLineSegment(sketch, "E360.top", {"start": v(-3.34, -116.88) * mm, "end": v(-378, -116.88) * mm});
            skLineSegment(sketch, "E360.left", {"start": v(-3.34, 90.13) * mm, "end": v(-3.34, -116.88) * mm});
            skLineSegment(sketch, "E360.right", {"start": v(-378, 90.13) * mm, "end": v(-378, -116.88) * mm});
            skPoint(sketch, "E361", {"position": v(-190.67, 90.13) * mm});
            skLineSegment(sketch, "E362", {"start": v(-197.02, 71.15) * mm, "end": v(-184.32, 71.15) * mm});
            skPoint(sketch, "E363", {"position": v(-190.67, 71.15) * mm});
            skSolve(sketch);
        }
        {
            var Q0;
            Q0=makeQuery(id+"F0.imprint","IMPRINT",FACE,{"disambiguationData":[TD([[makeQuery(id+"F0.imprint","IMPRINT",EDGE,{"derivedFrom":sQuery(id+"F0.wireOp",EDGE,"E0")}),1.0]])]});
            extrude(context, id + "F1", {"entities" : qUnion([Q0]), "depth" : 6.35 * mm});
        }
    });
